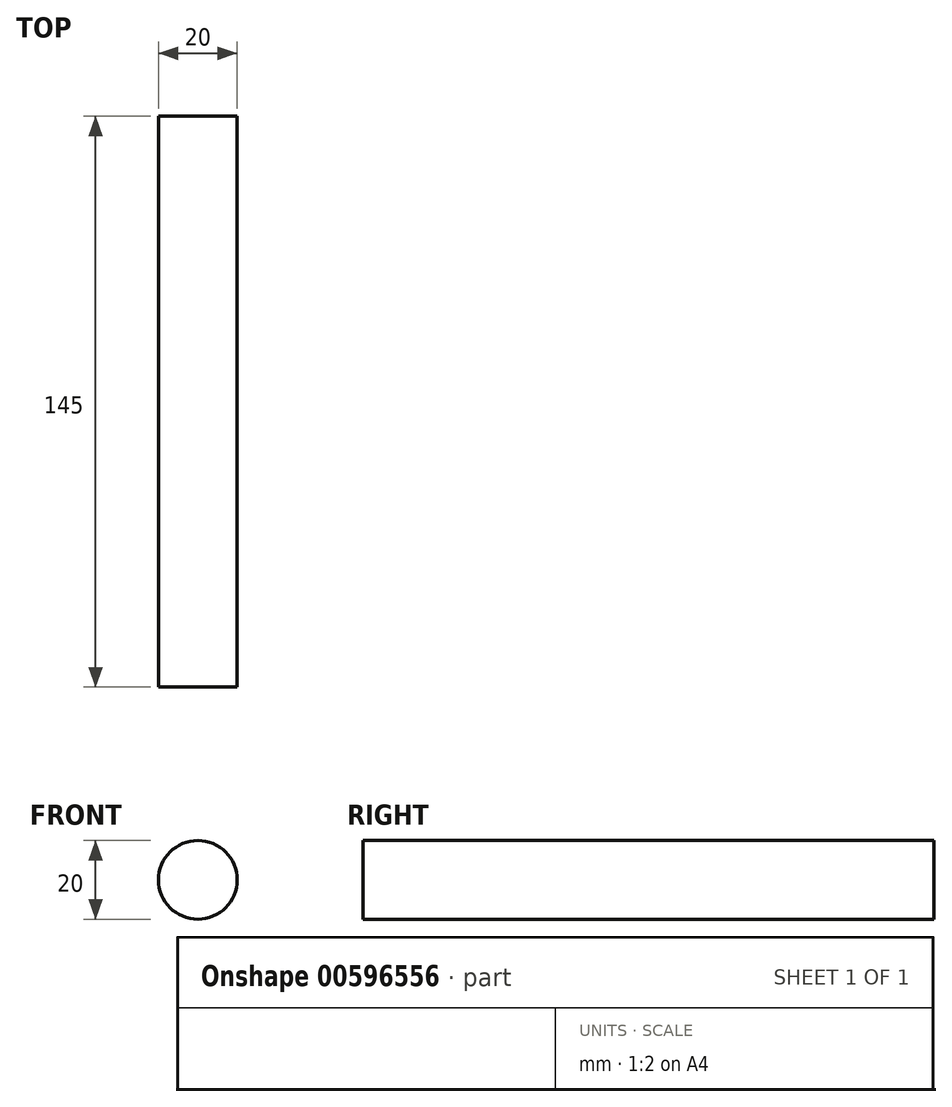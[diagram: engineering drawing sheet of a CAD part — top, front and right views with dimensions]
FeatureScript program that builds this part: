
annotation { "Feature Type Name" : "Feature", "Feature Type Description" : "" }
export const myFeature = defineFeature(function(context is Context, id is Id, definition is map)
    precondition{}
    {
        {
            var Q0;
            Q0=qCreatedBy(makeId("Front.planeOp"),FACE);
            var sketch = newSketch(context, id + "F0", { "sketchPlane" : qUnion([Q0])});
            skCircle(sketch, "E0", {"center": v(0, 0) * mm, "radius": 10 * mm});
            skSolve(sketch);
        }
        {
            var Q0;
            Q0=makeQuery(id+"F0.imprint","IMPRINT",FACE,{"disambiguationData":[TD([[makeQuery(id+"F0.imprint","IMPRINT",EDGE,{"derivedFrom":sQuery(id+"F0.wireOp",EDGE,"E0")}),1.0]])]});
            extrude(context, id + "F1", {"entities" : qUnion([Q0]), "depth" : 145 * mm, "offsetDistance" : 25 * mm});
        }
    });
